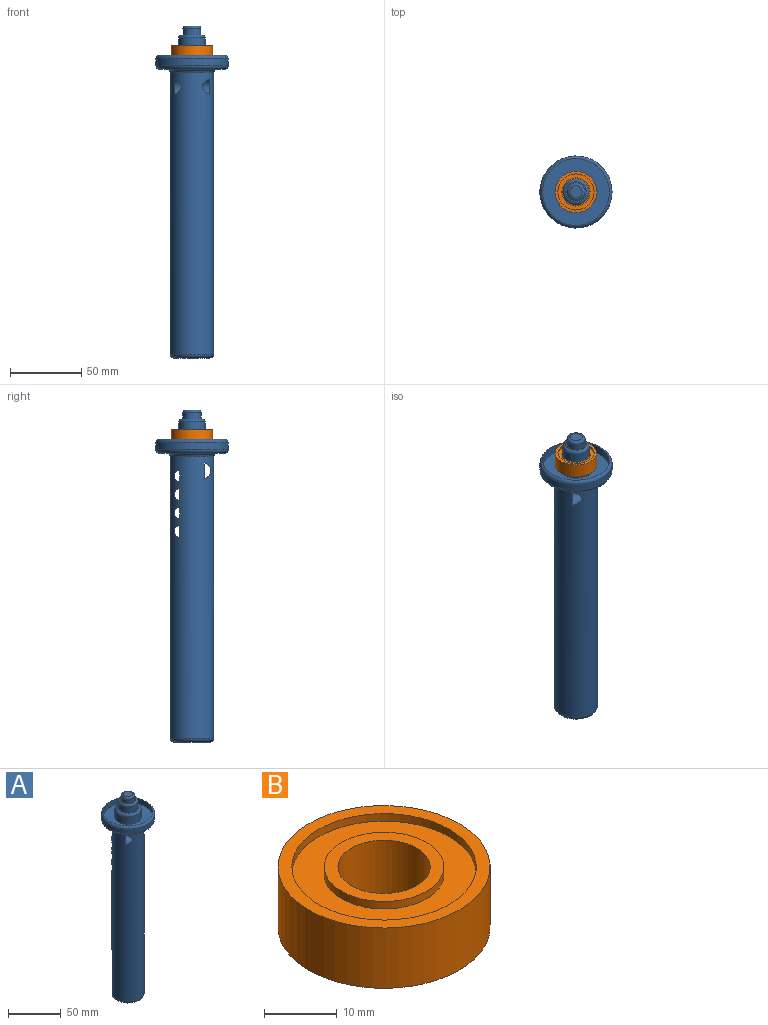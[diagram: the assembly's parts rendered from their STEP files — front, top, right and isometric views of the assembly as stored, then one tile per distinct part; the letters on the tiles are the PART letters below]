
ASSEMBLY  parts=2 mates=1
PART A: 34 faces, bbox 55x55x233.7 mm
  f0: cylinder r=25.4mm len=50.8mm, axis (0,0,-1), area 783.1mm2, adj f6,f12
  f1: plane 45.72x45.72mm, normal (0,0,-1), area 648.6mm2, adj f5,f6
  f2: cylinder r=15.24mm len=198.12mm, axis (0,0,1), area 18576.8mm2, adj f4,f5,f13,f14,f15,f16,f17,f18
  f3: plane 25.4x25.4mm, normal (0,0,-1), area 506.7mm2, adj f4
  f4: torus R=12.7mm, axis (0,0,-1), area 358.9mm2, adj f2,f3
  f5: torus R=17.78mm, axis (0,0,1), area 405.2mm2, adj f1,f2
  f6: torus R=22.86mm, axis (0,0,1), area 613.6mm2, adj f0,f1
  f7: cylinder r=23.49mm len=46.99mm, axis (0,0,-1), area 899.9mm2, adj f11,f12
  f8: plane 19.81x19.81mm, normal (0,0,1), area 38.3mm2, adj f9,f28
  f9: torus R=9.91mm, axis (0,0,1), area 288.9mm2, adj f8,f10
  f10: cylinder r=12.45mm len=24.89mm, axis (0,0,-1), area 695.2mm2, adj f9,f11
  f11: plane 46.99x46.99mm, normal (0,0,1), area 1247.6mm2, adj f7,f10
  f12: torus R=22.86mm, axis (0,0,1), area 520.1mm2, adj f0,f7
  f13: cylinder r=4.52mm len=25mm, axis (1,0,0), area 651.2mm2, adj f2,f14,f15
  f14: plane 9.03x5.21mm, normal (1,0,0), area 38.3mm2, adj f2,f13
  f15: plane 9.03x5.21mm, normal (-1,0,0), area 38.3mm2, adj f2,f13
  f16: cylinder r=5.5mm len=25mm, axis (1,0,0), area 772.1mm2, adj f2,f17,f18
  f17: plane 11x6.38mm, normal (1,0,0), area 57.2mm2, adj f2,f16
  f18: plane 11x6.38mm, normal (-1,0,0), area 57.2mm2, adj f2,f16
  f19: cylinder r=4.52mm len=25mm, axis (1,0,0), area 651.2mm2, adj f2,f20,f21
  f20: plane 9.03x5.21mm, normal (1,0,0), area 38.3mm2, adj f2,f19
  f21: plane 9.03x5.21mm, normal (-1,0,0), area 38.3mm2, adj f2,f19
  f22: cylinder r=4.52mm len=25mm, axis (1,0,0), area 651.2mm2, adj f2,f23,f24
  f23: plane 9.03x5.21mm, normal (1,0,0), area 38.3mm2, adj f2,f22
  f24: plane 9.03x5.21mm, normal (-1,0,0), area 38.3mm2, adj f2,f22
  f25: cylinder r=4.52mm len=25mm, axis (1,0,0), area 651.2mm2, adj f2,f26,f27
  f26: plane 9.03x5.21mm, normal (1,0,0), area 38.3mm2, adj f2,f25
  f27: plane 9.03x5.21mm, normal (-1,0,0), area 38.3mm2, adj f2,f25
  f28: cylinder r=9.27mm len=18.54mm, axis (0,0,-1), area 401.9mm2, adj f8,f30
  f29: plane 14.54x14.54mm, normal (0,0,1), area 39.4mm2, adj f30,f31
  f30: torus R=7.27mm, axis (0,0,1), area 168.7mm2, adj f28,f29
  f31: cylinder r=6.35mm len=12.7mm, axis (0,0,-1), area 175.6mm2, adj f29,f33
  f32: plane 8.7x8.7mm, normal (0,0,1), area 59.4mm2, adj f33
  f33: torus R=4.35mm, axis (0,0,1), area 111mm2, adj f31,f32
PART B: 12 faces, bbox 29.2x29.2x10.2 mm
  f0: plane 16.51x16.51mm, normal (0,0,-1), area 87.4mm2, adj f3,f9
  f1: plane 25.4x25.4mm, normal (0,0,1), area 292.6mm2, adj f4,f6
  f2: plane 29.21x29.21mm, normal (0,0,-1), area 163.4mm2, adj f7,f10
  f3: cylinder r=6.35mm len=12.7mm, axis (0,0,-1), area 405.4mm2, adj f0,f5
  f4: cylinder r=8.26mm len=16.51mm, axis (0,0,-1), area 65.9mm2, adj f1,f5
  f5: plane 16.51x16.51mm, normal (0,0,1), area 87.4mm2, adj f3,f4
  f6: cylinder r=12.7mm len=25.4mm, axis (0,0,-1), area 101.3mm2, adj f1,f8
  f7: cylinder r=14.61mm len=29.21mm, axis (0,0,-1), area 932.3mm2, adj f2,f8
  f8: plane 29.21x29.21mm, normal (0,0,1), area 163.4mm2, adj f6,f7
  f9: cylinder r=8.26mm len=16.51mm, axis (0,0,-1), area 65.9mm2, adj f0,f11
  f10: cylinder r=12.7mm len=25.4mm, axis (0,0,-1), area 101.3mm2, adj f2,f11
  f11: plane 25.4x25.4mm, normal (0,0,-1), area 292.6mm2, adj f9,f10
PLACE A t=(-4.89,2.32,9.1)mm fixed
PLACE B t=(-4.89,2.32,15.61)mm
MATE slider A.f9 <-> B.f6  axis (0,0,-1) through (-4.89,2.32,12.91)mm
